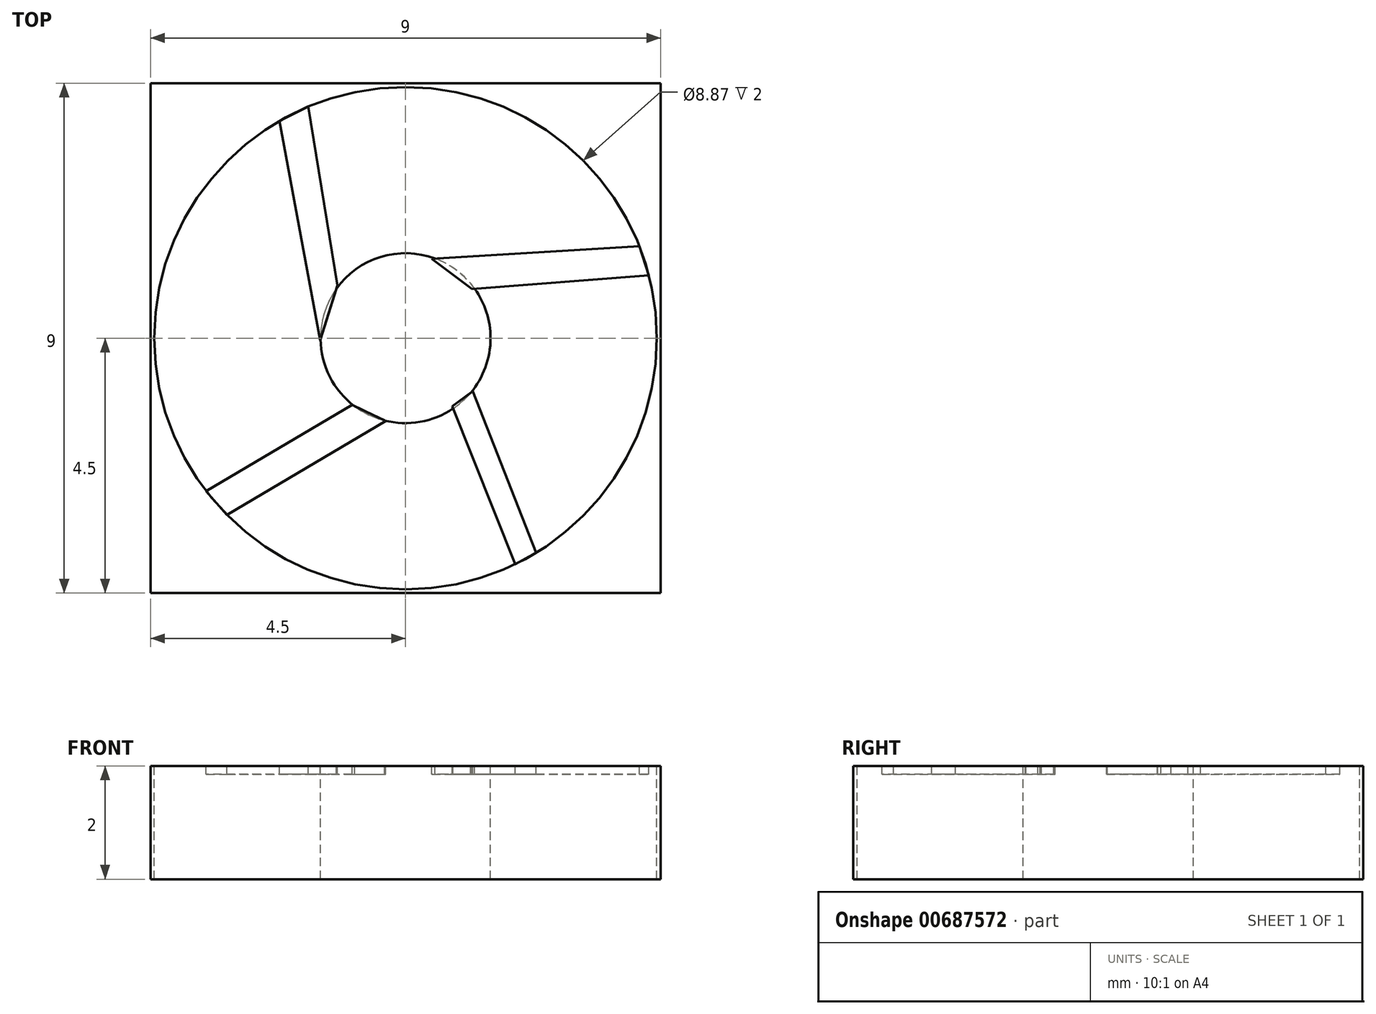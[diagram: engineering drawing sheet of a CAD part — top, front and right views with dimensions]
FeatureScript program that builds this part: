
annotation { "Feature Type Name" : "Feature", "Feature Type Description" : "" }
export const myFeature = defineFeature(function(context is Context, id is Id, definition is map)
    precondition{}
    {
        {
            var Q0;
            Q0=qCreatedBy(makeId("Top.planeOp"),FACE);
            var sketch = newSketch(context, id + "F0", { "sketchPlane" : qUnion([Q0])});
            skLineSegment(sketch, "E0.bottom", {"start": v(0, 0) * mm, "end": v(-9, 0) * mm});
            skLineSegment(sketch, "E0.top", {"start": v(0, 9) * mm, "end": v(-9, 9) * mm});
            skLineSegment(sketch, "E0.left", {"start": v(0, 0) * mm, "end": v(0, 9) * mm});
            skLineSegment(sketch, "E0.right", {"start": v(-9, 0) * mm, "end": v(-9, 9) * mm});
            skSolve(sketch);
        }
        {
            var Q0;
            Q0 = qSketchRegion(id + "F0", true);
            extrude(context, id + "F1", {"entities" : qUnion([Q0]), "depth" : 2 * mm, "offsetDistance" : 25 * mm});
        }
        {
            var Q0;
            Q0=makeQuery(id+"F1.opExtrude","CAP_FACE",FACE,{"disambiguationData":[OSD([sQuery(id+"F0.wireOp",EDGE,"E0.bottom"),sQuery(id+"F0.wireOp",EDGE,"E0.top"),sQuery(id+"F0.wireOp",EDGE,"E0.left"),sQuery(id+"F0.wireOp",EDGE,"E0.right")])],"isStart":false});
            var sketch = newSketch(context, id + "F2", { "sketchPlane" : qUnion([Q0])});
            skPoint(sketch, "E1.endSnap0", {"position": v(-9, 4.5) * mm});
            skCircle(sketch, "E2", {"center": v(-4.5, 4.5) * mm, "radius": 4.43 * mm});
            skPoint(sketch, "E1.start.orphan", {"position": v(-4.5, 9) * mm});
            skCircle(sketch, "E3", {"center": v(-4.5, 4.5) * mm, "radius": 1.5 * mm});
            skSolve(sketch);
        }
        {
            var Q0;
            Q0 = qSketchRegion(id + "F2", true);
            extrude(context, id + "F3", {"entities" : qUnion([Q0]), "operationType" : NewBodyOperationType.REMOVE, "oppositeDirection" : true, "depth" : 3 * mm, "offsetDistance" : 25 * mm});
        }
        {
            var Q0;
            {var subQ0=sQuery(id+"F0.wireOp",EDGE,"E0.left");var subQ1=sQuery(id+"F0.wireOp",EDGE,"E0.top");var subQ2=sQuery(id+"F0.wireOp",EDGE,"E0.right");var subQ3=sQuery(id+"F0.wireOp",EDGE,"E0.bottom");Q0=makeQuery(id+"F3.boolean.opBoolean","SPLIT",FACE,{"disambiguationData":[TD([makeQuery(id+"F1.opExtrude","SWEPT_FACE",FACE,{"disambiguationData":[OSD([subQ3])]})])],"derivedFrom":makeQuery(id+"F1.opExtrude","CAP_FACE",FACE,{"disambiguationData":[OSD([subQ3,subQ1,subQ0,subQ2])],"isStart":false})});}
            var sketch = newSketch(context, id + "F4", { "sketchPlane" : qUnion([Q0])});
            skPoint(sketch, "E4.orphan", {"position": v(-15.02, 4.84) * mm});
            skPoint(sketch, "E5.start.orphan", {"position": v(-5.44, 3.32) * mm});
            skPoint(sketch, "E6.end.orphan", {"position": v(-5.44, 4.84) * mm});
            skLineSegment(sketch, "E7", {"start": v(-6, 4.47) * mm, "end": v(-6.72, 8.33) * mm});
            skLineSegment(sketch, "E8", {"start": v(-6.72, 8.33) * mm, "end": v(-6.22, 8.59) * mm});
            skLineSegment(sketch, "E9", {"start": v(-6.22, 8.59) * mm, "end": v(-5.7, 5.43) * mm});
            skLineSegment(sketch, "E10", {"start": v(-5.7, 5.43) * mm, "end": v(-6, 4.47) * mm});
            skLineSegment(sketch, "E11", {"start": v(-4.04, 5.9) * mm, "end": v(-0.38, 6.13) * mm});
            skLineSegment(sketch, "E12", {"start": v(-0.38, 6.13) * mm, "end": v(-0.2, 5.6) * mm});
            skLineSegment(sketch, "E13", {"start": v(-0.2, 5.6) * mm, "end": v(-3.33, 5.37) * mm});
            skLineSegment(sketch, "E14", {"start": v(-3.33, 5.37) * mm, "end": v(-4.04, 5.9) * mm});
            skLineSegment(sketch, "E15", {"start": v(-5.44, 3.32) * mm, "end": v(-8.02, 1.8) * mm});
            skLineSegment(sketch, "E16", {"start": v(-8.02, 1.8) * mm, "end": v(-7.65, 1.38) * mm});
            skLineSegment(sketch, "E17", {"start": v(-7.65, 1.38) * mm, "end": v(-4.85, 3.04) * mm});
            skLineSegment(sketch, "E18", {"start": v(-3.68, 3.3) * mm, "end": v(-2.57, 0.51) * mm});
            skLineSegment(sketch, "E19", {"start": v(-2.57, 0.51) * mm, "end": v(-2.2, 0.71) * mm});
            skLineSegment(sketch, "E20", {"start": v(-2.2, 0.71) * mm, "end": v(-3.31, 3.56) * mm});
            skLineSegment(sketch, "E21", {"start": v(-3.31, 3.56) * mm, "end": v(-3.68, 3.3) * mm});
            skLineSegment(sketch, "E22", {"start": v(-5.44, 3.32) * mm, "end": v(-4.85, 3.04) * mm});
            skSolve(sketch);
        }
        {
            var Q0;
            Q0 = qSketchRegion(id + "F4", true);
            extrude(context, id + "F5", {"entities" : qUnion([Q0]), "operationType" : NewBodyOperationType.REMOVE, "oppositeDirection" : true, "depth" : 0.15 * mm, "offsetDistance" : 25 * mm});
        }
        {
            var Q0;
            Q0 = qSketchRegion(id + "F4", true);
            extrude(context, id + "F6", {"entities" : qUnion([Q0]), "oppositeDirection" : true, "depth" : 0.15 * mm, "offsetDistance" : 25 * mm});
        }
        {
            var Q0;
            {var subQ0=sQuery(id+"F0.wireOp",EDGE,"E0.left");var subQ1=sQuery(id+"F0.wireOp",EDGE,"E0.top");var subQ2=sQuery(id+"F0.wireOp",EDGE,"E0.right");var subQ3=sQuery(id+"F0.wireOp",EDGE,"E0.bottom");Q0=makeQuery(id+"F3.boolean.opBoolean","SPLIT",FACE,{"disambiguationData":[TD([makeQuery(id+"F1.opExtrude","SWEPT_FACE",FACE,{"disambiguationData":[OSD([subQ3])]})])],"derivedFrom":makeQuery(id+"F1.opExtrude","CAP_FACE",FACE,{"disambiguationData":[OSD([subQ3,subQ1,subQ0,subQ2])],"isStart":true})});}
            cPlane(context, id + "F7", {"entities" : qUnion([Q0]), "cplaneType" : CPlaneType.OFFSET, "offset" : 0 * mm, "width" : 150 * mm, "height" : 150 * mm});
        }
        {
            var Q0;
            Q0=qCreatedBy(id+"F7.planeOp",FACE);
            var sketch = newSketch(context, id + "F8", { "sketchPlane" : qUnion([Q0])});
            skFitSpline(sketch, "E23", {"points": [v(-3.2, -4.23) * mm, v(-2.4, -4.36) * mm, v(-1.7, -4.18) * mm, v(-0.15, -5.13) * mm], "startDerivative": vector(2.53, -0.8) * mm, "endDerivative": vector(2.58, -1.94) * mm});
            skPoint(sketch, "E24.2.internal.orphan", {"position": v(-1.7, -5.52) * mm});
            skPoint(sketch, "E25.3.internal.orphan", {"position": v(-2.47, -8.42) * mm});
            skPoint(sketch, "E26.end.orphan", {"position": v(-6.37, -8.42) * mm});
            skSolve(sketch);
        }
        {
            var Q0;
            {var subQ0=sQuery(id+"F0.wireOp",EDGE,"E0.left");var subQ1=sQuery(id+"F0.wireOp",EDGE,"E0.top");var subQ2=sQuery(id+"F0.wireOp",EDGE,"E0.right");var subQ3=sQuery(id+"F0.wireOp",EDGE,"E0.bottom");Q0=makeQuery(id+"F3.boolean.opBoolean","SPLIT",FACE,{"disambiguationData":[TD([makeQuery(id+"F1.opExtrude","SWEPT_FACE",FACE,{"disambiguationData":[OSD([subQ3])]})])],"derivedFrom":makeQuery(id+"F1.opExtrude","CAP_FACE",FACE,{"disambiguationData":[OSD([subQ3,subQ1,subQ0,subQ2])],"isStart":false})});}
            var sketch = newSketch(context, id + "F9", { "sketchPlane" : qUnion([Q0])});
            skFitSpline(sketch, "E27", {"points": [v(-3.2, 4.22) * mm, v(-2.41, 4.4) * mm, v(-1.73, 4.2) * mm, v(-0.12, 5.18) * mm], "startDerivative": vector(2.82, 1.1) * mm, "endDerivative": vector(4.03, 3.25) * mm});
            skSolve(sketch);
        }
        {
            var Q0;
            Q0=sQuery(id+"F9.wireOp",EDGE,"E27");
            var Q1;
            Q1=sQuery(id+"F8.wireOp",EDGE,"E23");
            loft(context, id + "F10", {"bodyType" : ToolBodyType.SURFACE, "wireProfilesArray" : [{ "wireProfileEntities" : qUnion([Q0]) }, { "wireProfileEntities" : qUnion([Q1]) }]});
        }
        {
            var Q0;
            Q0=makeQuery(id+"F10.opLoft","SWEPT_BODY",BODY,{"disambiguationData":[OSD([sQuery(id+"F8.wireOp",EDGE,"E23"),sQuery(id+"F9.wireOp",EDGE,"E27")])]});
            var Q1;
            Q1=makeQuery(id+"F3.boolean.opBoolean","COPY",FACE,{"derivedFrom":makeQuery(id+"F3.opExtrude","SWEPT_FACE",FACE,{"disambiguationData":[OSD([sQuery(id+"F2.wireOp",EDGE,"E3")])]})});
            circularPattern(context, id + "F11", {"entities" : qUnion([Q0]), "axis" : qUnion([Q1]), "angle" : 360 * degree, "instanceCount" : 15, "equalSpace" : true});
        }
    });
